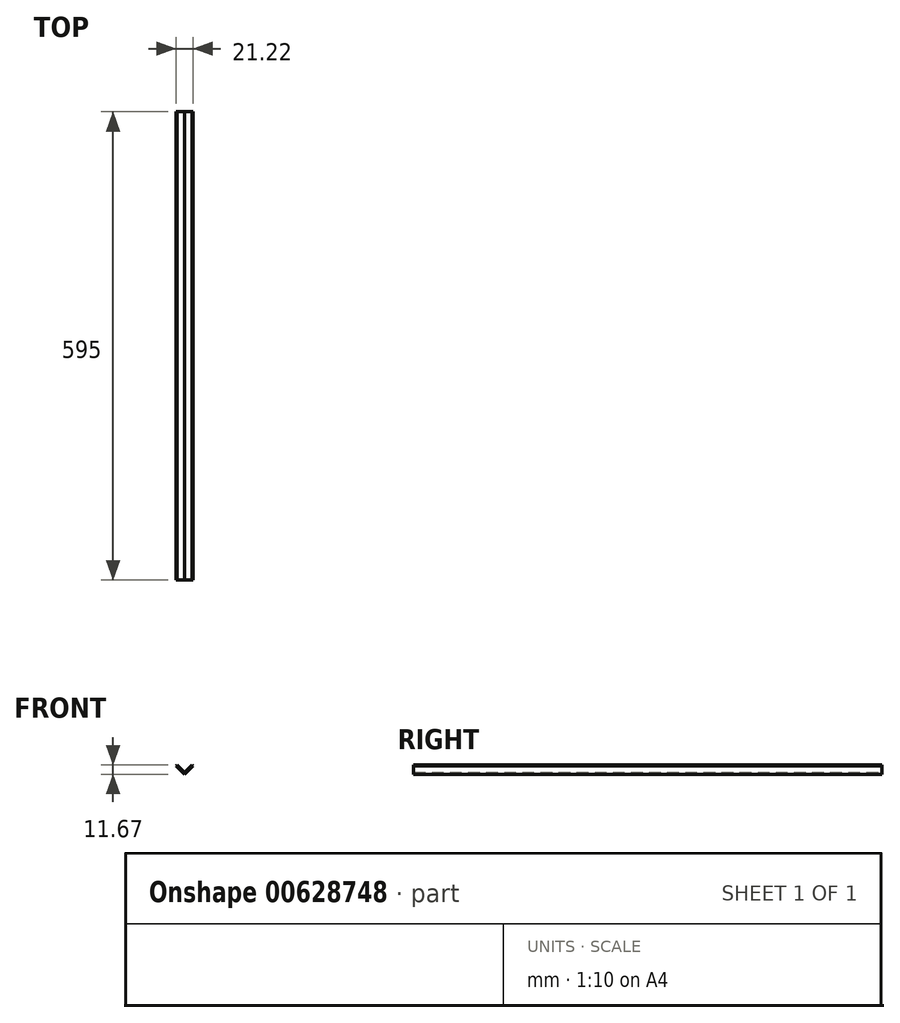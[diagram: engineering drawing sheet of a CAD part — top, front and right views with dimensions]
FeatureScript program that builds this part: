
annotation { "Feature Type Name" : "Feature", "Feature Type Description" : "" }
export const myFeature = defineFeature(function(context is Context, id is Id, definition is map)
    precondition{}
    {
        {
            var Q0;
            Q0=qCreatedBy(makeId("Front.planeOp"),FACE);
            var sketch = newSketch(context, id + "F0", { "sketchPlane" : qUnion([Q0])});
            skLineSegment(sketch, "E0", {"start": v(0, 0) * mm, "end": v(-9.55, 9.55) * mm});
            skLineSegment(sketch, "E1", {"start": v(-9.55, 9.55) * mm, "end": v(-10.6, 8.49) * mm});
            skLineSegment(sketch, "E2", {"start": v(-10.6, 8.49) * mm, "end": v(0, -2.12) * mm});
            skLineSegment(sketch, "E3", {"start": v(0, -2.12) * mm, "end": v(0, 0) * mm, "construction": true});
            skLineSegment(sketch, "E4.MirrorCS", {"start": v(0, 0) * mm, "end": v(9.55, 9.55) * mm});
            skLineSegment(sketch, "E5.MirrorCS", {"start": v(9.55, 9.55) * mm, "end": v(10.6, 8.49) * mm});
            skLineSegment(sketch, "E6.MirrorCS", {"start": v(10.6, 8.49) * mm, "end": v(0, -2.12) * mm});
            skSolve(sketch);
        }
        {
            var Q0;
            Q0=makeQuery(id+"F0.imprint","IMPRINT",FACE,{"disambiguationData":[TD([[makeQuery(id+"F0.imprint","IMPRINT",EDGE,{"derivedFrom":sQuery(id+"F0.wireOp",EDGE,"E0")}),1.0]])]});
            extrude(context, id + "F1", {"entities" : qUnion([Q0]), "depth" : 580 * mm + 15 * mm, "offsetDistance" : 25.4 * mm});
        }
    });
